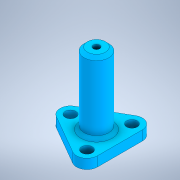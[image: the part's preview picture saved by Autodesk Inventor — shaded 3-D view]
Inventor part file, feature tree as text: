
AUTODESK INVENTOR PART (.ipt)
format: ipt  version: 2020 (Build 240168000, 168)  size: 152,064 bytes
history: native  units: mm
features: sketch x3, extrude x2, revolve x1, pattern_circular x1
ambient origin geometry x8: Origin, YZ Plane, XZ Plane, XY Plane, X Axis, Y Axis, Z Axis, Center Point
bodies: Solid1 (feature_tree)
feature tree (7):
  revolve  "Revolution1"  [1 undecoded]
  extrude  "Extrusion1"  Depth=25.0mm
  pattern_circular  "Circular Pattern1"  [2 undecoded]
  extrude  "Extrusion2"  Depth=10.0mm
  sketch  "Sketch1"  dims[d0=135.0deg d1=1.0mm]
  sketch  "Sketch2"  dims[d2=2.8mm d3=25.0mm]
  sketch  "Sketch3"  dims[d4=12.0mm d5=3.0mm d6=0.1mm d7=1.0mm d8=1.0mm d9=90.0deg d10=3.3mm d11=8.0mm d12=10.0mm d13=0.0mm d14=30.0mm d15=360.0deg d17=6.4mm d18=0.0mm d19=0.0mm]
note: 3 required parameter values undecoded (feature->parameter linkage not recoverable at this tier; creation-order binding heuristic only, values carry confidence <= 0.55)